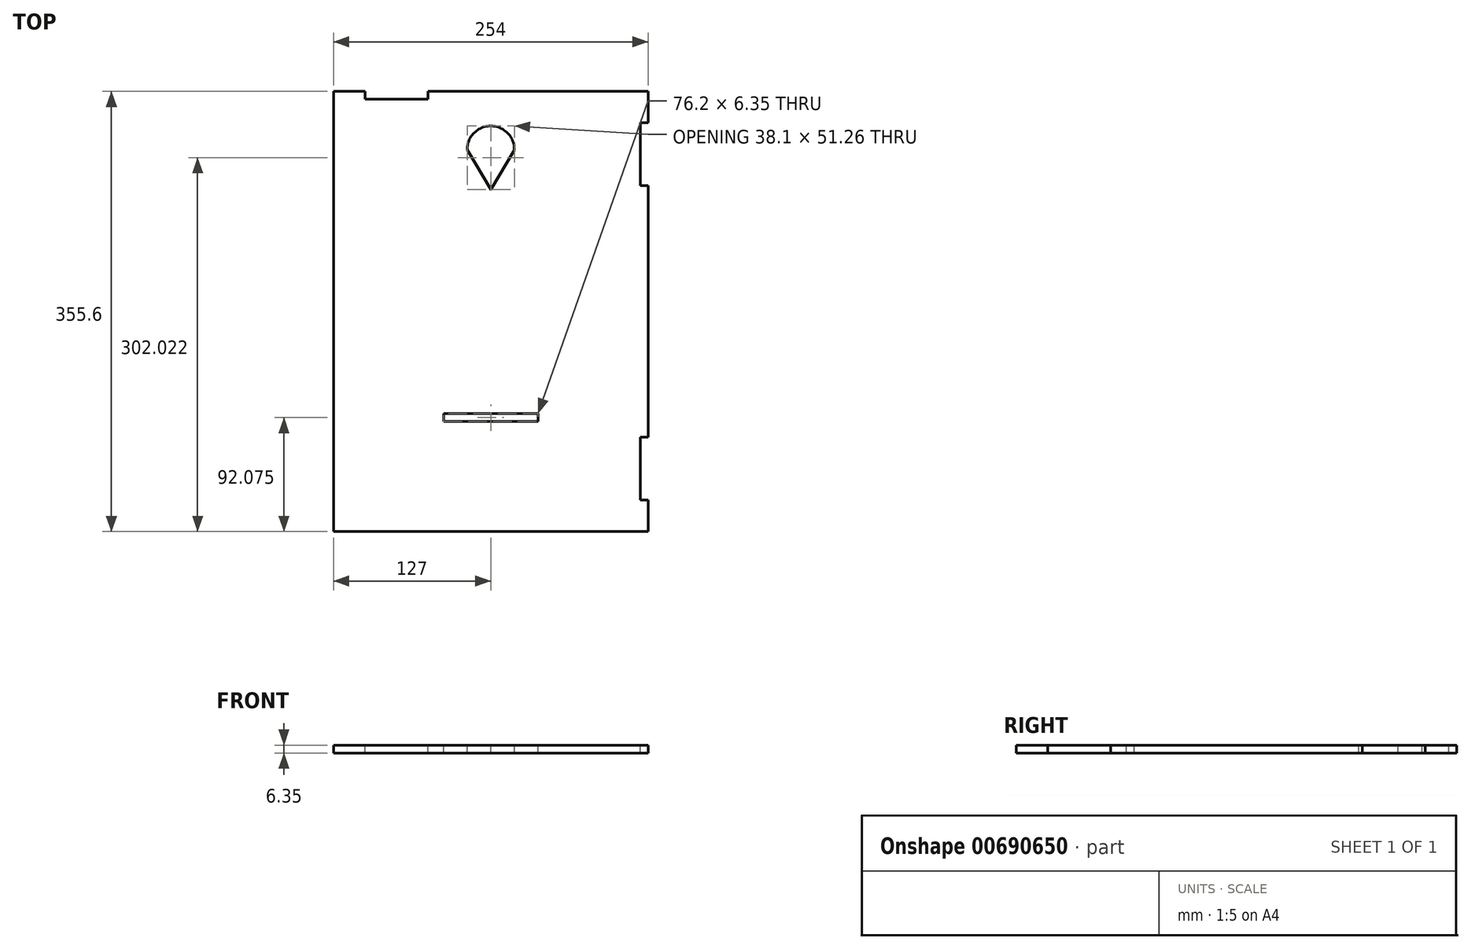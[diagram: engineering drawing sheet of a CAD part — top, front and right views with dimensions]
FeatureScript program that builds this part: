
annotation { "Feature Type Name" : "Feature", "Feature Type Description" : "" }
export const myFeature = defineFeature(function(context is Context, id is Id, definition is map)
    precondition{}
    {
        {
            var Q0;
            Q0=qCreatedBy(makeId("Top.planeOp"),FACE);
            var sketch = newSketch(context, id + "F0", { "sketchPlane" : qUnion([Q0])});
            skLineSegment(sketch, "E0.bottom", {"start": v(-127, 177.8) * mm, "end": v(127, 177.8) * mm});
            skLineSegment(sketch, "E0.top", {"start": v(-127, -177.8) * mm, "end": v(127, -177.8) * mm});
            skLineSegment(sketch, "E0.left", {"start": v(-127, 177.8) * mm, "end": v(-127, -177.8) * mm});
            skLineSegment(sketch, "E0.right", {"start": v(127, 177.8) * mm, "end": v(127, -177.8) * mm});
            skLineSegment(sketch, "E1", {"start": v(-127, 0) * mm, "end": v(127, 0) * mm, "construction": true});
            skSolve(sketch);
        }
        {
            var Q0;
            Q0 = qSketchRegion(id + "F0", true);
            extrude(context, id + "F1", {"entities" : qUnion([Q0]), "depth" : 6.35 * mm, "offsetDistance" : 25.4 * mm});
        }
        {
            var Q0;
            Q0=makeQuery(id+"F1.opExtrude","CAP_FACE",FACE,{"disambiguationData":[OSD([sQuery(id+"F0.wireOp",EDGE,"E0.bottom"),sQuery(id+"F0.wireOp",EDGE,"E0.top"),sQuery(id+"F0.wireOp",EDGE,"E0.left"),sQuery(id+"F0.wireOp",EDGE,"E0.right")])],"isStart":false});
            var sketch = newSketch(context, id + "F2", { "sketchPlane" : qUnion([Q0])});
            skLineSegment(sketch, "E2.bottom", {"start": v(-101.6, 177.8) * mm, "end": v(-50.8, 177.8) * mm});
            skLineSegment(sketch, "E2.top", {"start": v(-101.6, 171.45) * mm, "end": v(-50.8, 171.45) * mm});
            skLineSegment(sketch, "E2.left", {"start": v(-101.6, 177.8) * mm, "end": v(-101.6, 171.45) * mm});
            skLineSegment(sketch, "E2.right", {"start": v(-50.8, 177.8) * mm, "end": v(-50.8, 171.45) * mm});
            skSolve(sketch);
        }
        {
            var Q0;
            Q0 = qSketchRegion(id + "F2", true);
            extrude(context, id + "F3", {"entities" : qUnion([Q0]), "operationType" : NewBodyOperationType.REMOVE, "endBound" : BoundingType.THROUGH_ALL, "oppositeDirection" : true, "depth" : 25.4 * mm, "offsetDistance" : 25.4 * mm});
        }
        {
            var Q0;
            Q0=makeQuery(id+"F1.opExtrude","CAP_FACE",FACE,{"disambiguationData":[OSD([sQuery(id+"F0.wireOp",EDGE,"E0.bottom"),sQuery(id+"F0.wireOp",EDGE,"E0.top"),sQuery(id+"F0.wireOp",EDGE,"E0.left"),sQuery(id+"F0.wireOp",EDGE,"E0.right")])],"isStart":false});
            var sketch = newSketch(context, id + "F4", { "sketchPlane" : qUnion([Q0])});
            skLineSegment(sketch, "E3.bottom", {"start": v(127, 152.4) * mm, "end": v(120.65, 152.4) * mm});
            skLineSegment(sketch, "E3.top", {"start": v(127, 101.6) * mm, "end": v(120.65, 101.6) * mm});
            skLineSegment(sketch, "E3.left", {"start": v(127, 152.4) * mm, "end": v(127, 101.6) * mm});
            skLineSegment(sketch, "E3.right", {"start": v(120.65, 152.4) * mm, "end": v(120.65, 101.6) * mm});
            skLineSegment(sketch, "E4.MirrorCS", {"start": v(120.65, -152.4) * mm, "end": v(120.65, -101.6) * mm});
            skLineSegment(sketch, "E5.MirrorCS", {"start": v(127, -152.4) * mm, "end": v(127, -101.6) * mm});
            skLineSegment(sketch, "E6.MirrorCS", {"start": v(127, -101.6) * mm, "end": v(120.65, -101.6) * mm});
            skLineSegment(sketch, "E7.MirrorCS", {"start": v(127, -152.4) * mm, "end": v(120.65, -152.4) * mm});
            skSolve(sketch);
        }
        {
            var Q0;
            Q0 = qSketchRegion(id + "F4", true);
            extrude(context, id + "F5", {"entities" : qUnion([Q0]), "operationType" : NewBodyOperationType.REMOVE, "oppositeDirection" : true, "depth" : 25.4 * mm, "offsetDistance" : 25.4 * mm});
        }
        {
            var Q0;
            Q0=makeQuery(id+"F1.opExtrude","CAP_FACE",FACE,{"disambiguationData":[OSD([sQuery(id+"F0.wireOp",EDGE,"E0.bottom"),sQuery(id+"F0.wireOp",EDGE,"E0.top"),sQuery(id+"F0.wireOp",EDGE,"E0.left"),sQuery(id+"F0.wireOp",EDGE,"E0.right")])],"isStart":false});
            var sketch = newSketch(context, id + "F6", { "sketchPlane" : qUnion([Q0])});
            skLineSegment(sketch, "E8.bottom", {"start": v(-38.1, -82.55) * mm, "end": v(38.1, -82.55) * mm});
            skLineSegment(sketch, "E8.top", {"start": v(-38.1, -88.9) * mm, "end": v(38.1, -88.9) * mm});
            skLineSegment(sketch, "E8.left", {"start": v(-38.1, -82.55) * mm, "end": v(-38.1, -88.9) * mm});
            skLineSegment(sketch, "E8.right", {"start": v(38.1, -82.55) * mm, "end": v(38.1, -88.9) * mm});
            skLineSegment(sketch, "E9", {"start": v(0, -88.9) * mm, "end": v(0, -177.8) * mm, "construction": true});
            skSolve(sketch);
        }
        {
            var Q0;
            Q0 = qSketchRegion(id + "F6", true);
            extrude(context, id + "F7", {"entities" : qUnion([Q0]), "operationType" : NewBodyOperationType.REMOVE, "oppositeDirection" : true, "depth" : 25.4 * mm, "offsetDistance" : 25.4 * mm});
        }
        {
            var Q0;
            Q0=makeQuery(id+"F1.opExtrude","CAP_FACE",FACE,{"disambiguationData":[OSD([sQuery(id+"F0.wireOp",EDGE,"E0.bottom"),sQuery(id+"F0.wireOp",EDGE,"E0.top"),sQuery(id+"F0.wireOp",EDGE,"E0.left"),sQuery(id+"F0.wireOp",EDGE,"E0.right")])],"isStart":false});
            var sketch = newSketch(context, id + "F8", { "sketchPlane" : qUnion([Q0])});
            skLineSegment(sketch, "E10", {"start": v(-19.05, 130.49) * mm, "end": v(19.05, 130.49) * mm, "construction": true});
            skLineSegment(sketch, "E11", {"start": v(19.05, 130.49) * mm, "end": v(0, 98.6) * mm});
            skLineSegment(sketch, "E12", {"start": v(0, 98.6) * mm, "end": v(-19.05, 130.49) * mm});
            skArc(sketch, "E13", {"start": v(19.05, 130.49) * mm, "mid": v(0, 149.85) * mm, "end": v(-19.05, 130.49) * mm});
            skLineSegment(sketch, "E14", {"start": v(0, 149.85) * mm, "end": v(0, 177.8) * mm, "construction": true});
            skSolve(sketch);
        }
        {
            var Q0;
            Q0 = qSketchRegion(id + "F8", true);
            extrude(context, id + "F9", {"entities" : qUnion([Q0]), "operationType" : NewBodyOperationType.REMOVE, "oppositeDirection" : true, "depth" : 25.4 * mm, "offsetDistance" : 25.4 * mm});
        }
    });
